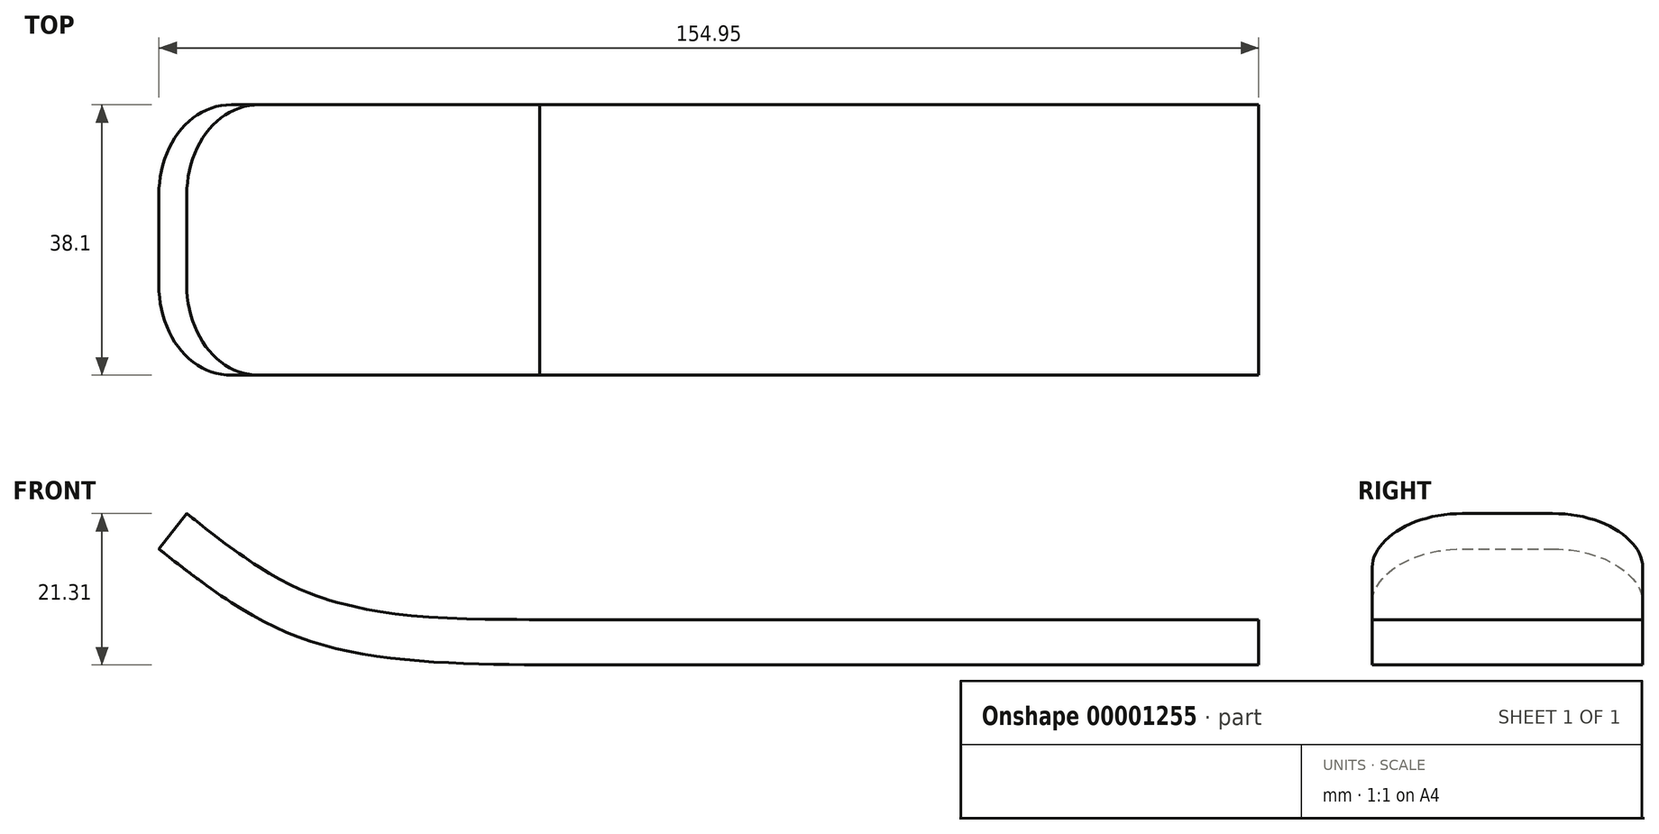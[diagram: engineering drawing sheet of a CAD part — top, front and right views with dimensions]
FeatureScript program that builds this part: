
annotation { "Feature Type Name" : "Feature", "Feature Type Description" : "" }
export const myFeature = defineFeature(function(context is Context, id is Id, definition is map)
    precondition{}
    {
        {
            var Q0;
            Q0=qCreatedBy(makeId("Front.planeOp"),FACE);
            var sketch = newSketch(context, id + "F0", { "sketchPlane" : qUnion([Q0])});
            skLineSegment(sketch, "E0", {"start": v(0, 0) * mm, "end": v(101.33, 0) * mm});
            skFitSpline(sketch, "E1", {"points": [v(0, 0) * mm, v(-32.65, 3.43) * mm, v(-53.62, 16.32) * mm], "startDerivative": vector(-65.14, 0.68) * mm, "endDerivative": vector(-41.55, 32.74) * mm});
            skLineSegment(sketch, "E2.0", {"start": v(0.03, 6.35) * mm, "end": v(101.33, 6.35) * mm});
            skFitSpline(sketch, "E2.1", {"points": [v(0.07, 6.35) * mm, v(-2.65, 6.38) * mm, v(-8.02, 6.43) * mm, v(-15.7, 6.74) * mm, v(-21.63, 7.36) * mm, v(-25.43, 8.05) * mm, v(-27.5, 8.53) * mm, v(-28.98, 8.92) * mm, v(-30.17, 9.3) * mm, v(-31.09, 9.6) * mm, v(-32.45, 10.11) * mm, v(-34.45, 10.97) * mm, v(-37.03, 12.3) * mm, v(-39.57, 13.83) * mm, v(-42.08, 15.52) * mm, v(-45.43, 17.95) * mm, v(-47.96, 19.95) * mm, v(-49.7, 21.31) * mm]});
            skLineSegment(sketch, "E3", {"start": v(-53.62, 16.32) * mm, "end": v(-49.7, 21.31) * mm});
            skLineSegment(sketch, "E4", {"start": v(101.33, 0) * mm, "end": v(101.33, 6.35) * mm});
            skSolve(sketch);
        }
        {
            var Q0;
            Q0 = qSketchRegion(id + "F0", true);
            extrude(context, id + "F1", {"entities" : qUnion([Q0]), "endBound" : BoundingType.SYMMETRIC, "depth" : 38.1 * mm});
        }
        {
            var Q0;
            Q0=makeQuery(id+"F1.opExtrude","CAP_EDGE",EDGE,{"disambiguationData":[OSD([sQuery(id+"F0.wireOp",EDGE,"E3")])],"isStart":true});
            var Q1;
            Q1=makeQuery(id+"F1.opExtrude","CAP_EDGE",EDGE,{"disambiguationData":[OSD([sQuery(id+"F0.wireOp",EDGE,"E3")])],"isStart":false});
            fillet(context, id + "F2", {"entities" : qUnion([Q0, Q1]), "radius" : 12.7 * mm, "tangentPropagation" : true, "allowEdgeOverflow" : false});
        }
    });
